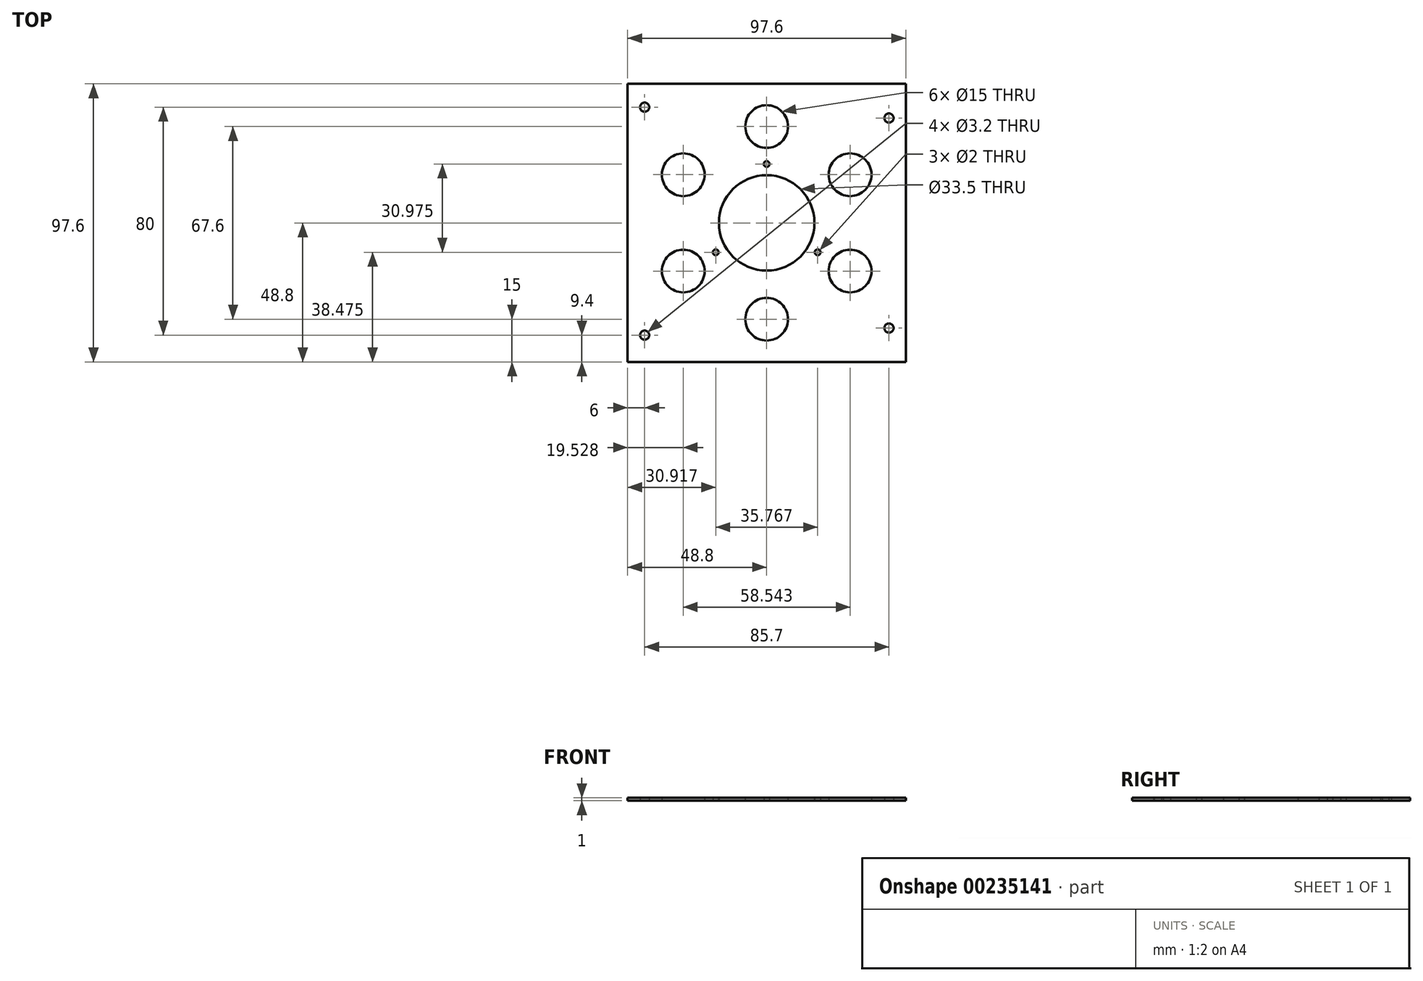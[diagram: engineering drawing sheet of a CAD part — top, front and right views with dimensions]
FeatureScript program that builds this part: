
annotation { "Feature Type Name" : "Feature", "Feature Type Description" : "" }
export const myFeature = defineFeature(function(context is Context, id is Id, definition is map)
    precondition{}
    {
        {
            var Q0;
            Q0=qCreatedBy(makeId("Top.planeOp"),FACE);
            var sketch = newSketch(context, id + "F0", { "sketchPlane" : qUnion([Q0])});
            skLineSegment(sketch, "E0.bottom", {"start": v(0, 0) * mm, "end": v(97.6, 0) * mm});
            skLineSegment(sketch, "E0.top", {"start": v(0, 97.6) * mm, "end": v(97.6, 97.6) * mm});
            skLineSegment(sketch, "E0.left", {"start": v(0, 0) * mm, "end": v(0, 97.6) * mm});
            skLineSegment(sketch, "E0.right", {"start": v(97.6, 0) * mm, "end": v(97.6, 97.6) * mm});
            skCircle(sketch, "E1", {"center": v(6, 9.4) * mm, "radius": 1.6 * mm});
            skCircle(sketch, "E2", {"center": v(48.8, 48.8) * mm, "radius": 16.75 * mm});
            skLineSegment(sketch, "E3", {"start": v(0, 48.8) * mm, "end": v(97.6, 48.8) * mm});
            skCircle(sketch, "E4", {"center": v(48.8, 69.45) * mm, "radius": 1 * mm});
            skCircle(sketch, "E5.1.0", {"center": v(30.92, 38.48) * mm, "radius": 1 * mm});
            skCircle(sketch, "E5.2.0", {"center": v(66.68, 38.47) * mm, "radius": 1 * mm});
            skCircle(sketch, "E6", {"center": v(91.7, 11.9) * mm, "radius": 1.6 * mm});
            skCircle(sketch, "E7", {"center": v(6, 89.4) * mm, "radius": 1.6 * mm});
            skCircle(sketch, "E8", {"center": v(91.7, 85.6) * mm, "radius": 1.6 * mm});
            skCircle(sketch, "E9", {"center": v(48.8, 82.6) * mm, "radius": 7.5 * mm});
            skCircle(sketch, "E10.1.0", {"center": v(19.53, 65.7) * mm, "radius": 7.5 * mm});
            skCircle(sketch, "E10.2.0", {"center": v(19.53, 31.9) * mm, "radius": 7.5 * mm});
            skCircle(sketch, "E10.3.0", {"center": v(48.8, 15) * mm, "radius": 7.5 * mm});
            skCircle(sketch, "E10.4.0", {"center": v(78.07, 31.9) * mm, "radius": 7.5 * mm});
            skCircle(sketch, "E10.5.0", {"center": v(78.07, 65.7) * mm, "radius": 7.5 * mm});
            skSolve(sketch);
        }
        {
            var Q0;
            Q0 = qSketchRegion(id + "F0", true);
            extrude(context, id + "F1", {"entities" : qUnion([Q0]), "depth" : 1 * mm});
        }
    });
